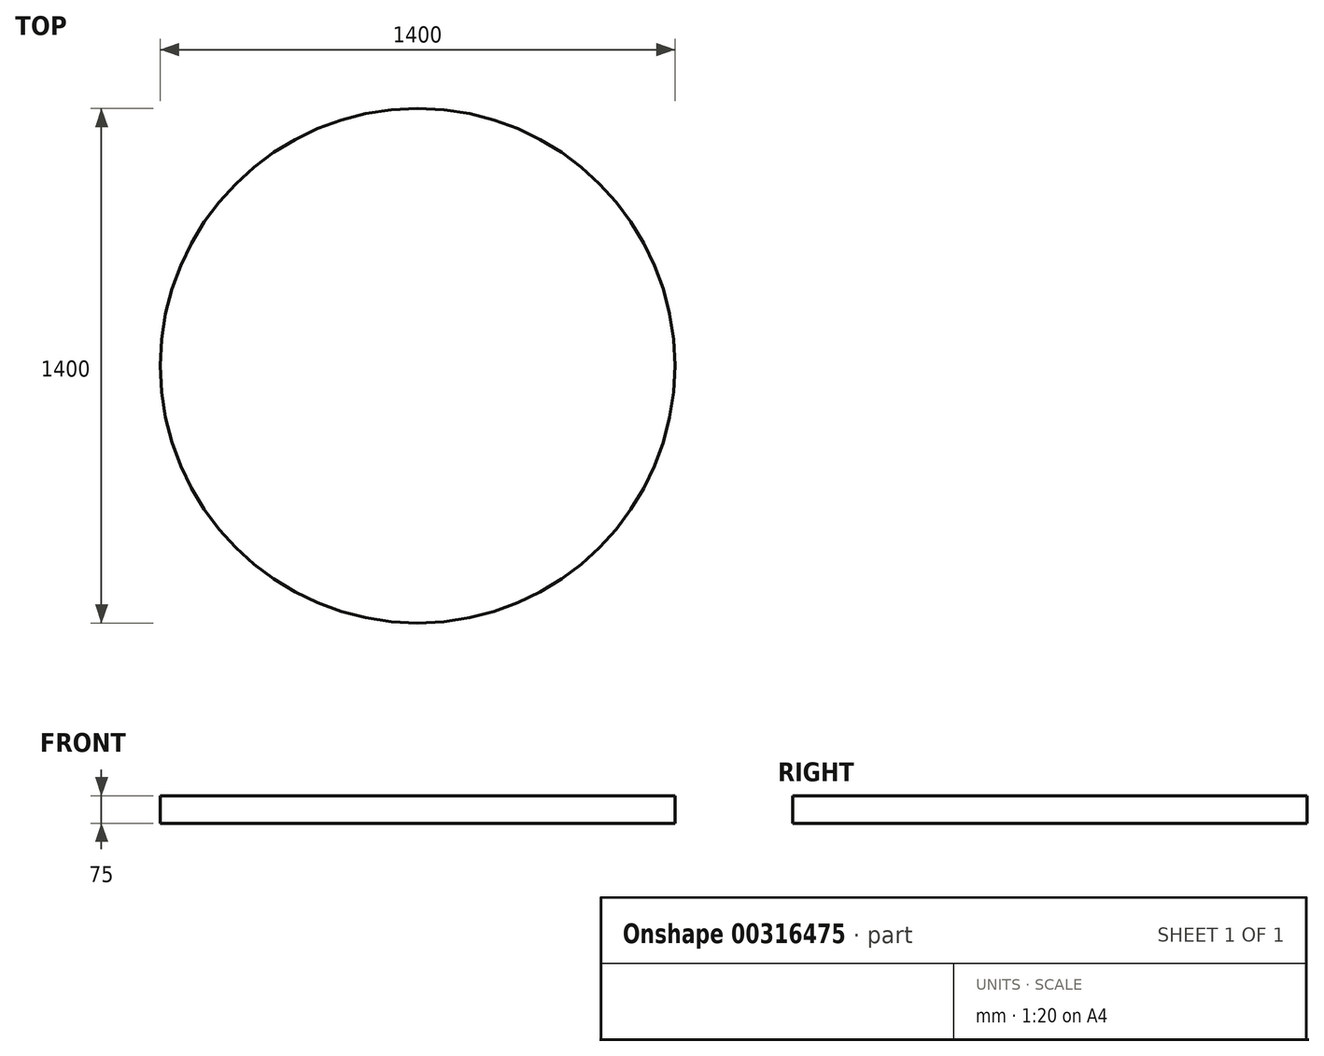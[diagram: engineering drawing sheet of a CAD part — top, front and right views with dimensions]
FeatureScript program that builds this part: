
annotation { "Feature Type Name" : "Feature", "Feature Type Description" : "" }
export const myFeature = defineFeature(function(context is Context, id is Id, definition is map)
    precondition{}
    {
        {
            var Q0;
            Q0=qCreatedBy(makeId("Top.planeOp"),FACE);
            var sketch = newSketch(context, id + "F0", { "sketchPlane" : qUnion([Q0])});
            skCircle(sketch, "E0", {"center": v(0, 0) * mm, "radius": 700 * mm});
            skSolve(sketch);
        }
        {
            var Q0;
            Q0=makeQuery(id+"F0.imprint","IMPRINT",FACE,{"disambiguationData":[TD([[makeQuery(id+"F0.imprint","IMPRINT",EDGE,{"derivedFrom":sQuery(id+"F0.wireOp",EDGE,"E0")}),1.0]])]});
            extrude(context, id + "F1", {"entities" : qUnion([Q0]), "oppositeDirection" : true, "depth" : 75 * mm});
        }
    });
